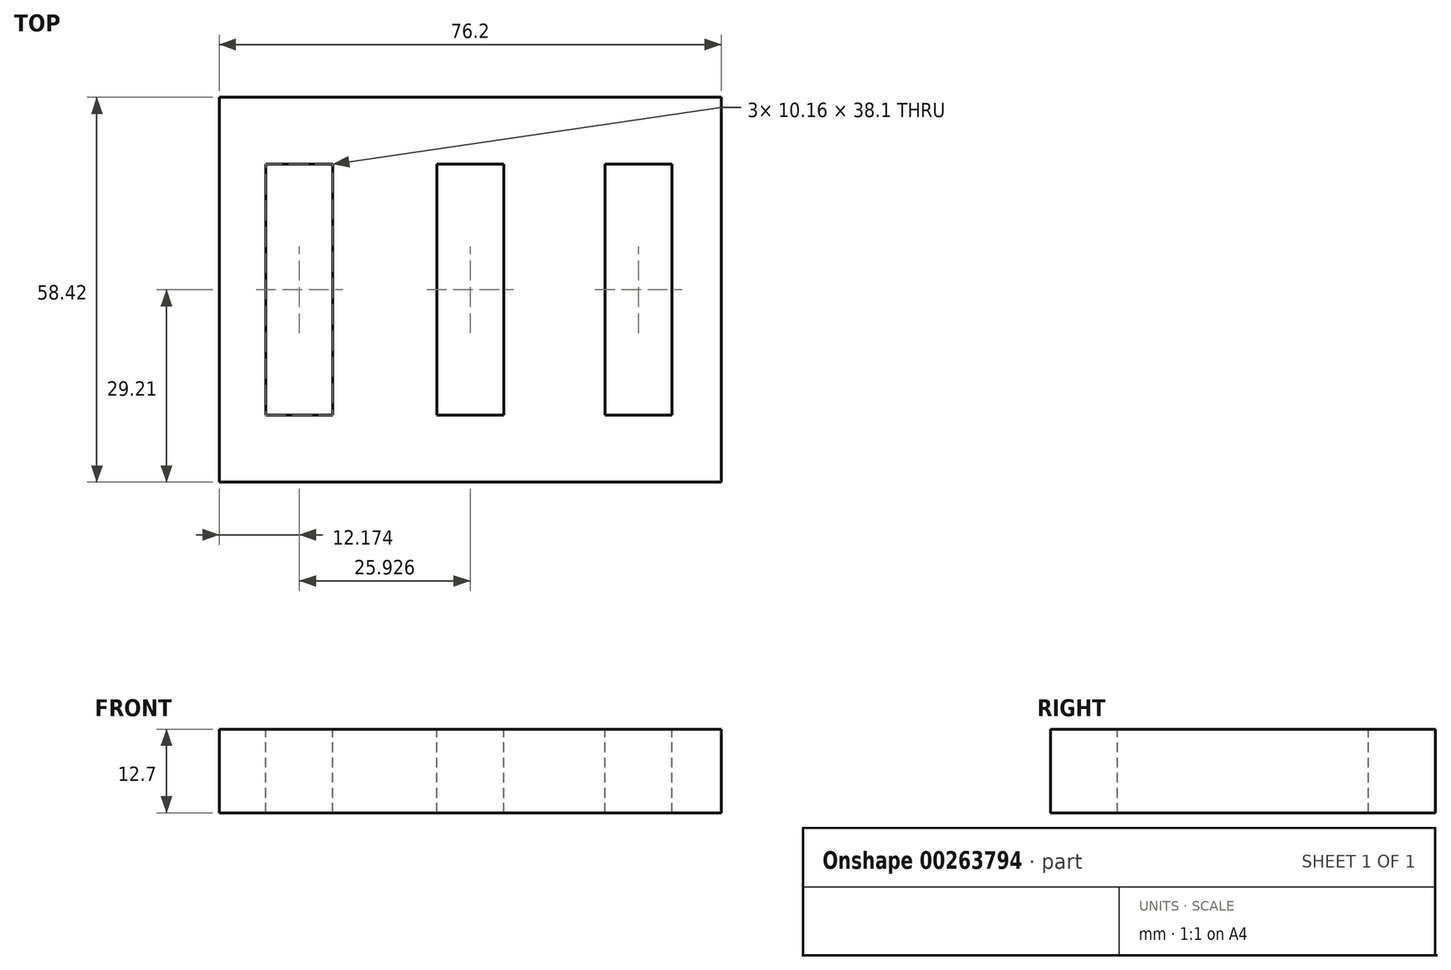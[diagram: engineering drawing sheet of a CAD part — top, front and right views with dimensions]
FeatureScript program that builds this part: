
annotation { "Feature Type Name" : "Feature", "Feature Type Description" : "" }
export const myFeature = defineFeature(function(context is Context, id is Id, definition is map)
    precondition{}
    {
        {
            var Q0;
            Q0=qCreatedBy(makeId("Top.planeOp"),FACE);
            var sketch = newSketch(context, id + "F0", { "sketchPlane" : qUnion([Q0])});
            skLineSegment(sketch, "E0.bottom", {"start": v(38.1, 29.21) * mm, "end": v(-38.1, 29.21) * mm});
            skLineSegment(sketch, "E0.top", {"start": v(38.1, -29.21) * mm, "end": v(-38.1, -29.21) * mm});
            skLineSegment(sketch, "E0.left", {"start": v(38.1, 29.21) * mm, "end": v(38.1, -29.21) * mm});
            skLineSegment(sketch, "E0.right", {"start": v(-38.1, 29.21) * mm, "end": v(-38.1, -29.21) * mm});
            skPoint(sketch, "E0.middle", {"position": v(0, 0) * mm});
            skSolve(sketch);
        }
        {
            var Q0;
            Q0 = qSketchRegion(id + "F0", true);
            extrude(context, id + "F1", {"entities" : qUnion([Q0]), "depth" : 12.7 * mm});
        }
        {
            var Q0;
            Q0=makeQuery(id+"F1.opExtrude","CAP_FACE",FACE,{"disambiguationData":[OSD([sQuery(id+"F0.wireOp",EDGE,"E0.bottom"),sQuery(id+"F0.wireOp",EDGE,"E0.top"),sQuery(id+"F0.wireOp",EDGE,"E0.left"),sQuery(id+"F0.wireOp",EDGE,"E0.right")])],"isStart":false});
            var sketch = newSketch(context, id + "F2", { "sketchPlane" : qUnion([Q0])});
            skLineSegment(sketch, "E1.bottom", {"start": v(5.08, -19.05) * mm, "end": v(-5.08, -19.05) * mm});
            skLineSegment(sketch, "E1.top", {"start": v(5.08, 19.05) * mm, "end": v(-5.08, 19.05) * mm});
            skLineSegment(sketch, "E1.left", {"start": v(5.08, -19.05) * mm, "end": v(5.08, 19.05) * mm});
            skLineSegment(sketch, "E1.right", {"start": v(-5.08, -19.05) * mm, "end": v(-5.08, 19.05) * mm});
            skPoint(sketch, "E1.middle", {"position": v(0, 0) * mm});
            skLineSegment(sketch, "E2.bottom", {"start": v(20.46, 19.05) * mm, "end": v(30.62, 19.05) * mm});
            skLineSegment(sketch, "E2.top", {"start": v(20.46, -19.05) * mm, "end": v(30.62, -19.05) * mm});
            skLineSegment(sketch, "E2.left", {"start": v(20.46, 19.05) * mm, "end": v(20.46, -19.05) * mm});
            skLineSegment(sketch, "E2.right", {"start": v(30.62, 19.05) * mm, "end": v(30.62, -19.05) * mm});
            skPoint(sketch, "E2.middle", {"position": v(25.54, 0) * mm});
            skLineSegment(sketch, "E3.bottom", {"start": v(-31, 19.05) * mm, "end": v(-20.85, 19.05) * mm});
            skLineSegment(sketch, "E3.top", {"start": v(-31, -19.05) * mm, "end": v(-20.85, -19.05) * mm});
            skLineSegment(sketch, "E3.left", {"start": v(-31, 19.05) * mm, "end": v(-31, -19.05) * mm});
            skLineSegment(sketch, "E3.right", {"start": v(-20.85, 19.05) * mm, "end": v(-20.85, -19.05) * mm});
            skPoint(sketch, "E3.middle", {"position": v(-25.93, 0) * mm});
            skSolve(sketch);
        }
        {
            var Q0;
            Q0 = qSketchRegion(id + "F2", true);
            extrude(context, id + "F3", {"entities" : qUnion([Q0]), "operationType" : NewBodyOperationType.REMOVE, "endBound" : BoundingType.THROUGH_ALL, "oppositeDirection" : true, "depth" : 25.4 * mm});
        }
    });
